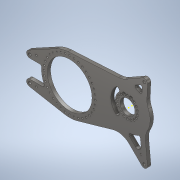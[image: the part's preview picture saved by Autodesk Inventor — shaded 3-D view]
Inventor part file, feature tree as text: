
AUTODESK INVENTOR PART (.ipt)
format: ipt  version: 2021 (Build 250183000, 183)  size: 527,360 bytes
history: native  units: in
note: dims shown in document units (in); Inventor stores cm internally (conversion verified against a paired STEP export)
features: sketch x13, extrude x10, hole x3, projected_geometry x3, chamfer x1, fillet x1
ambient origin geometry x8: Origin, YZ Plane, XZ Plane, XY Plane, X Axis, Y Axis, Z Axis, Center Point
bodies: Body1 (feature_tree)
feature tree (31):
  extrude  "Extrusion24"  Depth=2.16in
  extrude  "Extrusion28"  Depth=9.0in
  hole  "Hole9"  [1 undecoded]
  hole  "Hole11"  [1 undecoded]
  hole  "Hole13"  [1 undecoded]
  extrude  "Extrusion30"  Depth=1.5in
  extrude  "Extrusion31"  Depth=0.5in
  extrude  "Extrusion32"  Depth=0.25in
  extrude  "Extrusion33"  Depth=7.75in
  extrude  "Extrusion34"  Depth=0.25in
  chamfer  "Chamfer2"  Distance=1.0in
  sketch  "Sketch58"  dims[d289=17.223in d290=7.75in]
  extrude  "Extrusion42"  Depth=0.25in
  extrude  "Extrusion46"  Depth=0.25in
  fillet  "Fillet6"  Radius=0.3972in
  sketch  "Sketch71"  dims[d295=0.257in d296=0.75in d297=0.438in d298=0.25in d299=0.5635in d300=1.0in d301=0.8108in d302=0.1718in]
  extrude  "Extrusion50"  Depth=0.25in
  sketch  "Sketch2"  dims[d9=8.5in d92=2.16in]
  sketch  "Sketch35"  dims[d118=0.75in d119=0.75in d120=0.75in d121=0.75in d137=9.0in d142=6.5in]
  projected_geometry  "Projected Loop2"
  sketch  "Sketch36"  dims[d143=1.0in d210=1.0in]
  sketch  "Sketch40"  dims[d211=6.0in d212=6.0in]
  sketch  "Sketch43"  dims[d213=3.718in d214=1.0in]
  sketch  "Sketch47"  dims[d235=10.718in d237=1.5in]
  sketch  "Sketch48"  dims[d239=0.5in d240=0.0in d266=6.75in]
  sketch  "Sketch49"  dims[d267=0.5in d268=0.0in]
  sketch  "Sketch50"  dims[d269=0.386in d270=0.75in d271=0.762in d272=0.25in d273=0.5635in d274=0.484in d275=0.8108in d288=5.0in]
  sketch  "Sketch67"  dims[d291=3.5433in d293=360.0deg]
  sketch  "Sketch72"  dims[d303=15.0deg d316=1.0in d317=0.0481in d318=1.0in d319=0.3972in d322=0.271in d323=0.1355in d324=0.5in d325=0.266in d326=0.75in d327=0.507in d328=0.25in d329=0.5635in d330=1.0in d331=0.8108in d347=1.0in d348=0.0in d349=0.75in d350=0.75in d351=0.5in d353=0.75in d354=0.75in d355=0.25in d356=1.0in d357=0.0in d358=0.25in d359=1.0in d360=0.0in d361=1.0in d362=1.0in d363=0.25in d364=1.0in d365=0.0in d366=2.5in d367=1.0in d368=0.0in d373=0.0156in d374=0.125in d375=45.0deg d435=1.0in d436=0.0in d456=2.25in d457=8.715in d466=3.7in d467=5.0in d468=45.0deg d469=1.5in d470=1.0in d471=0.0in d472=0.25in d502=0.315in d503=1.0in d504=0.0in]
  projected_geometry  "Project Cut Edges2"
  projected_geometry  "Project Cut Edges4"
note: 3 required parameter values undecoded (feature->parameter linkage not recoverable at this tier; creation-order binding heuristic only, values carry confidence <= 0.55)
